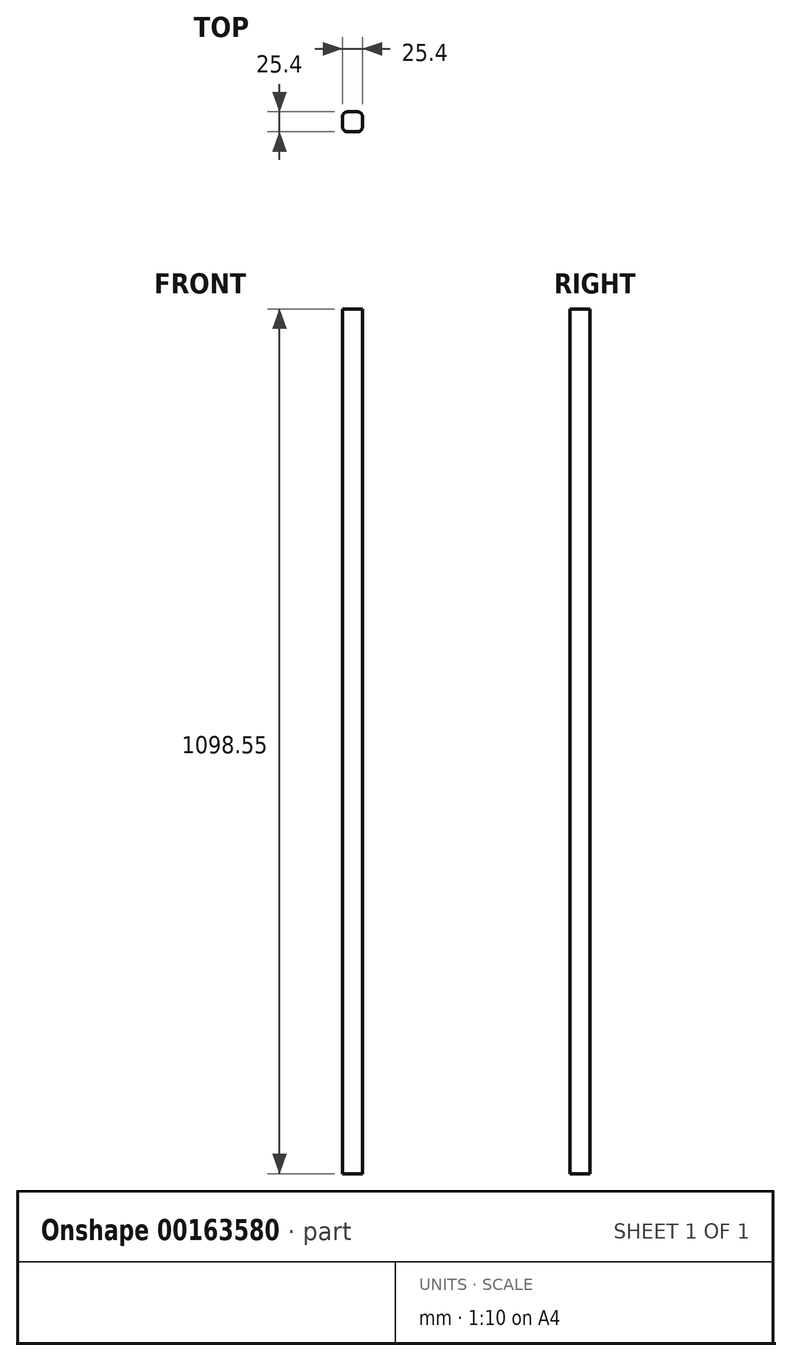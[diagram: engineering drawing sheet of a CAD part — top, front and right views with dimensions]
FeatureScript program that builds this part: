
annotation { "Feature Type Name" : "Feature", "Feature Type Description" : "" }
export const myFeature = defineFeature(function(context is Context, id is Id, definition is map)
    precondition{}
    {
        {
            var Q0;
            Q0=qCreatedBy(makeId("Top.planeOp"),FACE);
            var sketch = newSketch(context, id + "F0", { "sketchPlane" : qUnion([Q0])});
            skLineSegment(sketch, "E0.bottom", {"start": v(6.35, 12.7) * mm, "end": v(-6.35, 12.7) * mm});
            skLineSegment(sketch, "E0.top", {"start": v(6.35, -12.7) * mm, "end": v(-6.35, -12.7) * mm});
            skLineSegment(sketch, "E0.left", {"start": v(12.7, 6.35) * mm, "end": v(12.7, -6.35) * mm});
            skLineSegment(sketch, "E0.right", {"start": v(-12.7, 6.35) * mm, "end": v(-12.7, -6.35) * mm});
            skPoint(sketch, "E0.middle", {"position": v(0, 0) * mm});
            skPoint(sketch, "E1.visualSharp", {"position": v(-12.7, 12.7) * mm});
            skArc(sketch, "E1.filletArc", {"start": v(-6.35, 12.7) * mm, "mid": v(-10.84, 10.84) * mm, "end": v(-12.7, 6.35) * mm});
            skPoint(sketch, "E2.visualSharp", {"position": v(-12.7, -12.7) * mm});
            skArc(sketch, "E2.filletArc", {"start": v(-12.7, -6.35) * mm, "mid": v(-10.84, -10.84) * mm, "end": v(-6.35, -12.7) * mm});
            skPoint(sketch, "E3.visualSharp", {"position": v(12.7, -12.7) * mm});
            skArc(sketch, "E3.filletArc", {"start": v(6.35, -12.7) * mm, "mid": v(10.84, -10.84) * mm, "end": v(12.7, -6.35) * mm});
            skPoint(sketch, "E4.visualSharp", {"position": v(12.7, 12.7) * mm});
            skArc(sketch, "E4.filletArc", {"start": v(12.7, 6.35) * mm, "mid": v(10.84, 10.84) * mm, "end": v(6.35, 12.7) * mm});
            skSolve(sketch);
        }
        {
            var Q0;
            Q0=qSketchRegion(id+"F0",true);
            extrude(context, id + "F1", {"entities" : qUnion([Q0]), "depth" : 1098.55 * mm, "offsetDistance" : 25.4 * mm});
        }
    });
